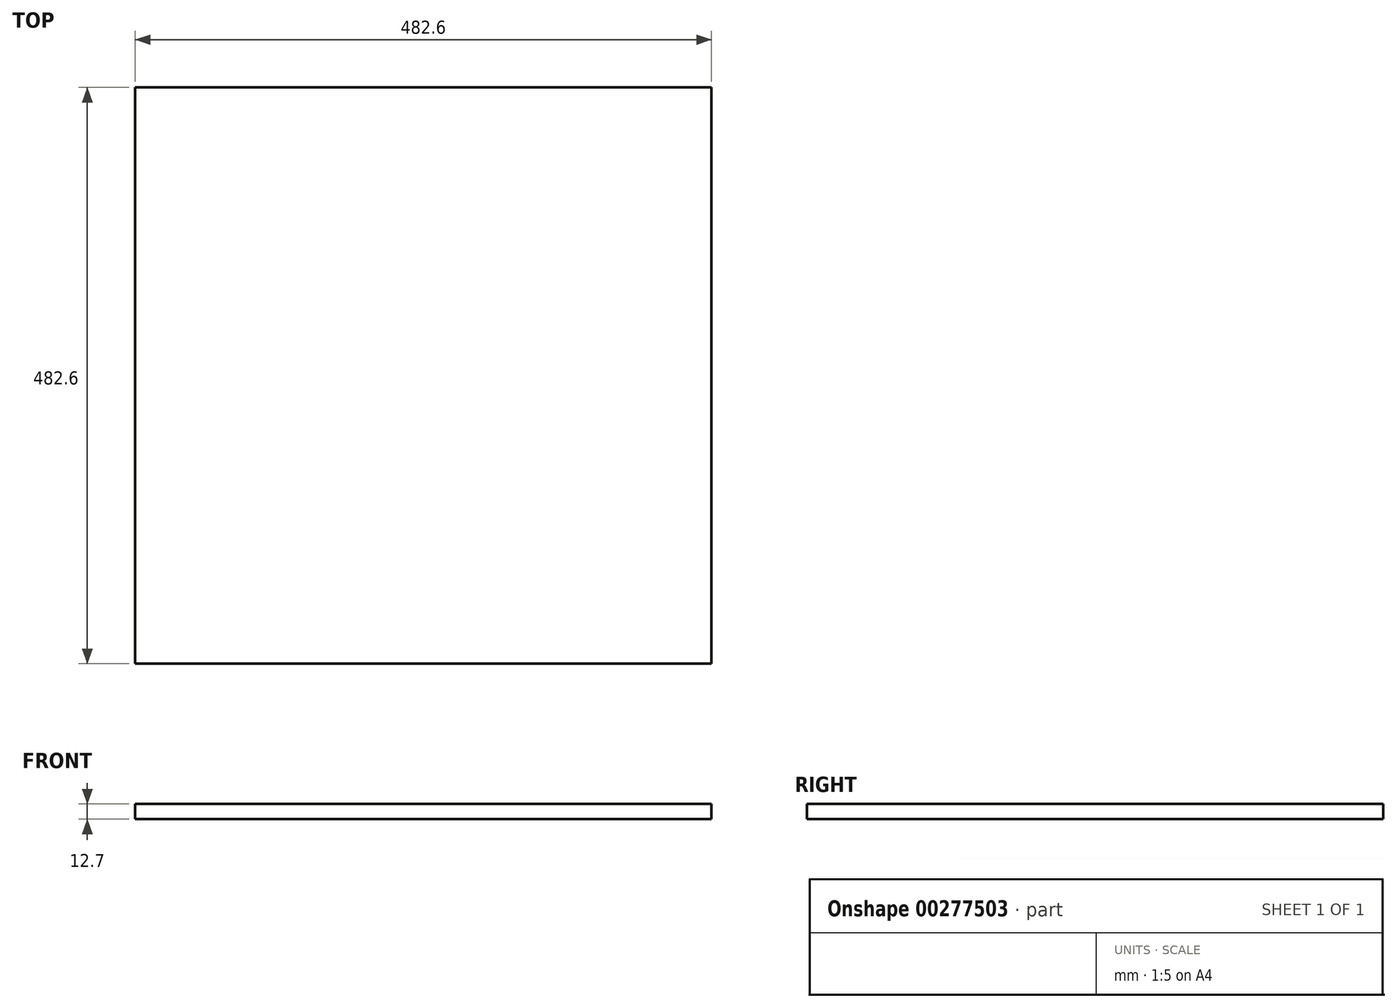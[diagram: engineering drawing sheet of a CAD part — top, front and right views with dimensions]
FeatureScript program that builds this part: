
annotation { "Feature Type Name" : "Feature", "Feature Type Description" : "" }
export const myFeature = defineFeature(function(context is Context, id is Id, definition is map)
    precondition{}
    {
        {
            var Q0;
            Q0=qCreatedBy(makeId("Top.planeOp"),FACE);
            var sketch = newSketch(context, id + "F0", { "sketchPlane" : qUnion([Q0])});
            skLineSegment(sketch, "E0.bottom", {"start": v(-155.54, -240.5) * mm, "end": v(327.06, -240.5) * mm});
            skLineSegment(sketch, "E0.top", {"start": v(-155.54, 242.1) * mm, "end": v(327.06, 242.1) * mm});
            skLineSegment(sketch, "E0.left", {"start": v(-155.54, -240.5) * mm, "end": v(-155.54, 242.1) * mm});
            skLineSegment(sketch, "E0.right", {"start": v(327.06, -240.5) * mm, "end": v(327.06, 242.1) * mm});
            skSolve(sketch);
        }
        {
            var Q0;
            Q0 = qSketchRegion(id + "F0", true);
            extrude(context, id + "F1", {"entities" : qUnion([Q0]), "depth" : 12.7 * mm});
        }
    });
